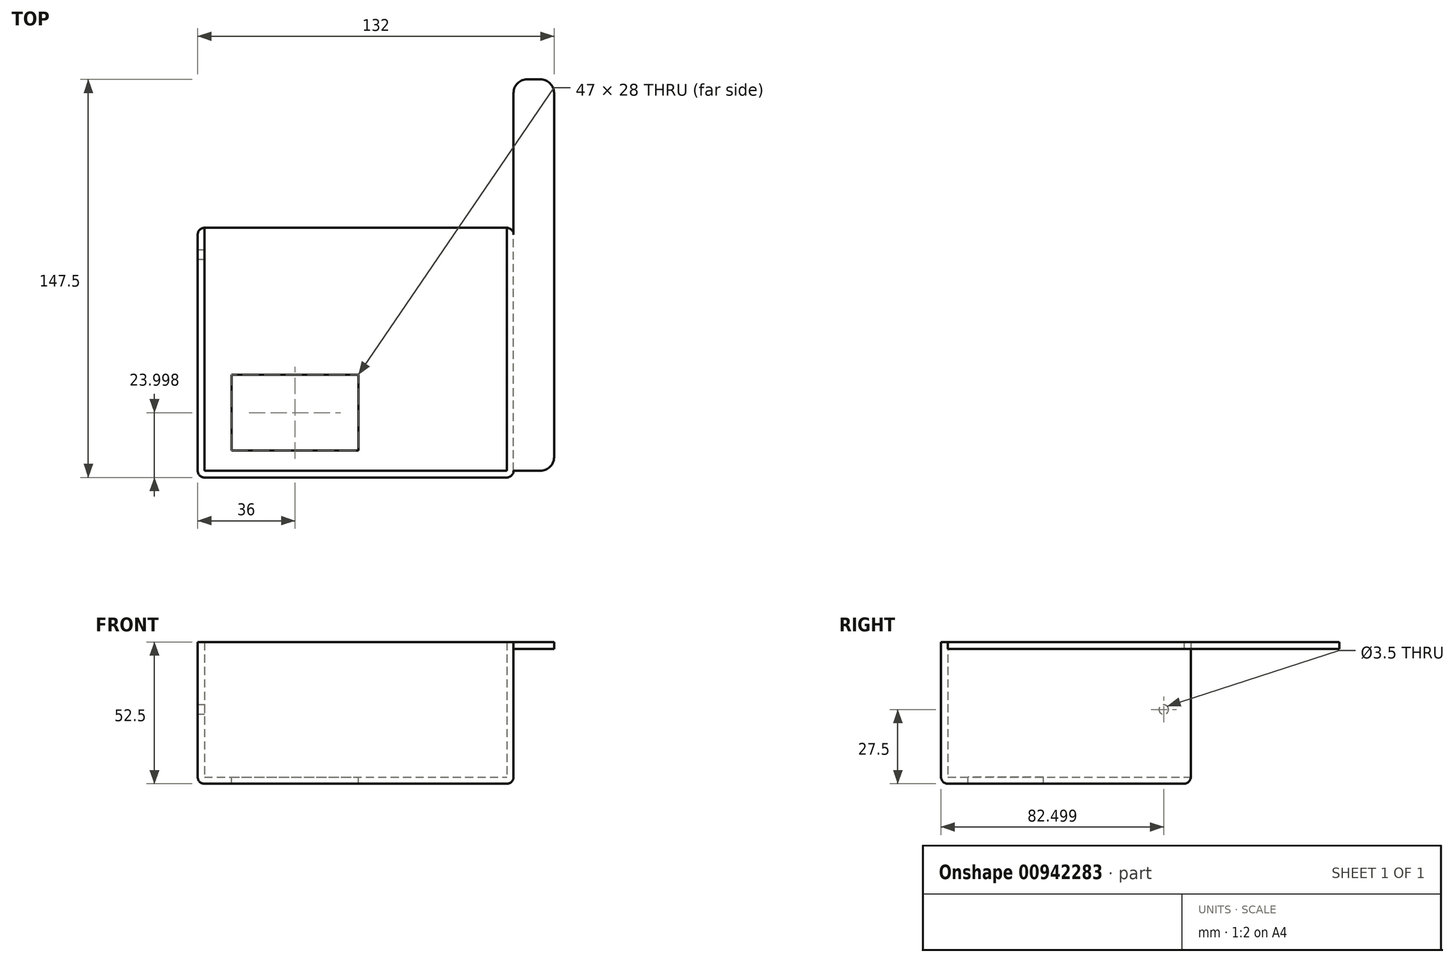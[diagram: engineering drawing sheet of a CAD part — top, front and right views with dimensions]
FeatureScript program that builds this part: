
annotation { "Feature Type Name" : "Feature", "Feature Type Description" : "" }
export const myFeature = defineFeature(function(context is Context, id is Id, definition is map)
    precondition{}
    {
        {
            var Q0;
            Q0=qCreatedBy(makeId("Top.planeOp"),FACE);
            var sketch = newSketch(context, id + "F0", { "sketchPlane" : qUnion([Q0])});
            skLineSegment(sketch, "E0.bottom", {"start": v(-58.5, 52.88) * mm, "end": v(58.5, 52.88) * mm});
            skLineSegment(sketch, "E0.top", {"start": v(-58.5, -39.62) * mm, "end": v(58.5, -39.62) * mm});
            skLineSegment(sketch, "E0.left", {"start": v(-58.5, 52.88) * mm, "end": v(-58.5, -39.62) * mm});
            skLineSegment(sketch, "E0.right", {"start": v(58.5, 52.88) * mm, "end": v(58.5, -39.62) * mm});
            skSolve(sketch);
        }
        {
            var Q0;
            Q0=makeQuery(id+"F0.imprint","IMPRINT",FACE,{"disambiguationData":[TD([[makeQuery(id+"F0.imprint","IMPRINT",EDGE,{"derivedFrom":sQuery(id+"F0.wireOp",EDGE,"E0.bottom")}),-1.0]])]});
            extrude(context, id + "F1", {"entities" : qUnion([Q0]), "depth" : 2.5 * mm, "offsetDistance" : 25 * mm});
        }
        {
            var Q0;
            Q0=makeQuery(id+"F1.opExtrude","CAP_FACE",FACE,{"disambiguationData":[OSD([sQuery(id+"F0.wireOp",EDGE,"E0.bottom"),sQuery(id+"F0.wireOp",EDGE,"E0.top"),sQuery(id+"F0.wireOp",EDGE,"E0.left"),sQuery(id+"F0.wireOp",EDGE,"E0.right")])],"isStart":false});
            var sketch = newSketch(context, id + "F2", { "sketchPlane" : qUnion([Q0])});
            skLineSegment(sketch, "E1.bottom", {"start": v(-46, -1.62) * mm, "end": v(1, -1.62) * mm});
            skLineSegment(sketch, "E1.top", {"start": v(-46, -29.62) * mm, "end": v(1, -29.62) * mm});
            skLineSegment(sketch, "E1.left", {"start": v(-46, -1.62) * mm, "end": v(-46, -29.62) * mm});
            skLineSegment(sketch, "E1.right", {"start": v(1, -1.62) * mm, "end": v(1, -29.62) * mm});
            skLineSegment(sketch, "E2.bottom", {"start": v(-58.5, -39.62) * mm, "end": v(58.5, -39.62) * mm});
            skLineSegment(sketch, "E2.top", {"start": v(-58.5, -37.12) * mm, "end": v(58.5, -37.12) * mm});
            skLineSegment(sketch, "E2.left", {"start": v(-58.5, -39.62) * mm, "end": v(-58.5, -37.12) * mm});
            skLineSegment(sketch, "E2.right", {"start": v(58.5, -39.62) * mm, "end": v(58.5, -37.12) * mm});
            skLineSegment(sketch, "E3.bottom", {"start": v(-58.5, -37.12) * mm, "end": v(-56, -37.12) * mm});
            skLineSegment(sketch, "E3.top", {"start": v(-58.5, 52.88) * mm, "end": v(-56, 52.88) * mm});
            skLineSegment(sketch, "E3.left", {"start": v(-58.5, -37.12) * mm, "end": v(-58.5, 52.88) * mm});
            skLineSegment(sketch, "E3.right", {"start": v(-56, -37.12) * mm, "end": v(-56, 52.88) * mm});
            skLineSegment(sketch, "E4.bottom", {"start": v(58.5, -37.12) * mm, "end": v(56, -37.12) * mm});
            skLineSegment(sketch, "E4.top", {"start": v(58.5, 52.88) * mm, "end": v(56, 52.88) * mm});
            skLineSegment(sketch, "E4.left", {"start": v(58.5, -37.12) * mm, "end": v(58.5, 52.88) * mm});
            skLineSegment(sketch, "E4.right", {"start": v(56, -37.12) * mm, "end": v(56, 52.88) * mm});
            skSolve(sketch);
        }
        {
            var Q0;
            Q0=makeQuery(id+"F2.imprint","IMPRINT",FACE,{"disambiguationData":[TD([[makeQuery(id+"F2.imprint","IMPRINT",EDGE,{"derivedFrom":sQuery(id+"F2.wireOp",EDGE,"E4.top")}),-1.0]])]});
            var Q1;
            Q1=makeQuery(id+"F2.imprint","IMPRINT",FACE,{"disambiguationData":[TD([[makeQuery(id+"F2.imprint","IMPRINT",EDGE,{"derivedFrom":sQuery(id+"F2.wireOp",EDGE,"E2.bottom")}),1.0]])]});
            var Q2;
            Q2=makeQuery(id+"F2.imprint","IMPRINT",FACE,{"disambiguationData":[TD([[makeQuery(id+"F2.imprint","IMPRINT",EDGE,{"derivedFrom":sQuery(id+"F2.wireOp",EDGE,"E3.top")}),-1.0]])]});
            extrude(context, id + "F3", {"entities" : qUnion([Q0, Q1, Q2]), "operationType" : NewBodyOperationType.ADD, "depth" : 50 * mm, "offsetDistance" : 25 * mm});
        }
        {
            var Q0;
            Q0=makeQuery(id+"F2.imprint","IMPRINT",FACE,{"disambiguationData":[TD([[makeQuery(id+"F2.imprint","IMPRINT",EDGE,{"derivedFrom":sQuery(id+"F2.wireOp",EDGE,"E1.bottom")}),-1.0]])]});
            extrude(context, id + "F4", {"entities" : qUnion([Q0]), "operationType" : NewBodyOperationType.REMOVE, "oppositeDirection" : true, "depth" : 25 * mm, "offsetDistance" : 25 * mm});
        }
        {
            var Q0;
            Q0=makeQuery(id+"F3.boolean.opBoolean","MERGE",FACE,{"derivedFrom":[makeQuery(id+"F1.opExtrude","SWEPT_FACE",FACE,{"disambiguationData":[OSD([sQuery(id+"F0.wireOp",EDGE,"E0.left")])]}),makeQuery(id+"F3.opExtrude","SWEPT_FACE",FACE,{"disambiguationData":[OSD([sQuery(id+"F2.wireOp",EDGE,"E2.left"),sQuery(id+"F2.wireOp",EDGE,"E3.left")])]})]});
            var sketch = newSketch(context, id + "F5", { "sketchPlane" : qUnion([Q0])});
            skCircle(sketch, "E5", {"center": v(-42.88, 27.5) * mm, "radius": 1.75 * mm});
            skSolve(sketch);
        }
        {
            var Q0;
            Q0 = qSketchRegion(id + "F5", true);
            extrude(context, id + "F6", {"entities" : qUnion([Q0]), "operationType" : NewBodyOperationType.REMOVE, "oppositeDirection" : true, "depth" : 25 * mm, "offsetDistance" : 25 * mm});
        }
        {
            var Q0;
            Q0=makeQuery(id+"F1.opExtrude","CAP_EDGE",EDGE,{"disambiguationData":[OSD([sQuery(id+"F0.wireOp",EDGE,"E0.left")])],"isStart":true});
            var Q1;
            Q1=makeQuery(id+"F3.boolean.opBoolean","MERGE",EDGE,{"derivedFrom":[makeQuery(id+"F1.opExtrude","SWEPT_EDGE",EDGE,{"disambiguationData":[OSD([sQuery(id+"F0.wireOp",EDGE,"E0.top"),sQuery(id+"F0.wireOp",EDGE,"E0.left")])]}),makeQuery(id+"F3.opExtrude","SWEPT_EDGE",EDGE,{"disambiguationData":[OSD([sQuery(id+"F2.wireOp",EDGE,"E2.bottom"),sQuery(id+"F2.wireOp",EDGE,"E2.left")])]})]});
            var Q2;
            Q2=makeQuery(id+"F1.opExtrude","CAP_EDGE",EDGE,{"disambiguationData":[OSD([sQuery(id+"F0.wireOp",EDGE,"E0.top")])],"isStart":true});
            var Q3;
            Q3=makeQuery(id+"F1.opExtrude","CAP_EDGE",EDGE,{"disambiguationData":[OSD([sQuery(id+"F0.wireOp",EDGE,"E0.right")])],"isStart":true});
            var Q4;
            Q4=makeQuery(id+"F3.boolean.opBoolean","MERGE",EDGE,{"derivedFrom":[makeQuery(id+"F1.opExtrude","SWEPT_EDGE",EDGE,{"disambiguationData":[OSD([sQuery(id+"F0.wireOp",EDGE,"E0.top"),sQuery(id+"F0.wireOp",EDGE,"E0.right")])]}),makeQuery(id+"F3.opExtrude","SWEPT_EDGE",EDGE,{"disambiguationData":[OSD([sQuery(id+"F2.wireOp",EDGE,"E2.bottom"),sQuery(id+"F2.wireOp",EDGE,"E2.right")])]})]});
            var Q5;
            Q5=makeQuery(id+"F1.opExtrude","CAP_EDGE",EDGE,{"disambiguationData":[OSD([sQuery(id+"F0.wireOp",EDGE,"E0.bottom")])],"isStart":true});
            var Q6;
            Q6=makeQuery(id+"F3.boolean.opBoolean","MERGE",EDGE,{"derivedFrom":[makeQuery(id+"F1.opExtrude","SWEPT_EDGE",EDGE,{"disambiguationData":[OSD([sQuery(id+"F0.wireOp",EDGE,"E0.bottom"),sQuery(id+"F0.wireOp",EDGE,"E0.left")])]}),makeQuery(id+"F3.opExtrude","SWEPT_EDGE",EDGE,{"disambiguationData":[OSD([sQuery(id+"F2.wireOp",EDGE,"E3.top"),sQuery(id+"F2.wireOp",EDGE,"E3.left")])]})]});
            var Q7;
            Q7=makeQuery(id+"F3.boolean.opBoolean","MERGE",EDGE,{"derivedFrom":[makeQuery(id+"F1.opExtrude","SWEPT_EDGE",EDGE,{"disambiguationData":[OSD([sQuery(id+"F0.wireOp",EDGE,"E0.bottom"),sQuery(id+"F0.wireOp",EDGE,"E0.right")])]}),makeQuery(id+"F3.opExtrude","SWEPT_EDGE",EDGE,{"disambiguationData":[OSD([sQuery(id+"F2.wireOp",EDGE,"E4.top"),sQuery(id+"F2.wireOp",EDGE,"E4.left")])]})]});
            fillet(context, id + "F7", {"entities" : qUnion([Q0, Q1, Q2, Q3, Q4, Q5, Q6, Q7]), "radius" : 2.5 * mm, "tangentPropagation" : true, "allowEdgeOverflow" : false});
        }
        {
            var Q0;
            Q0=makeQuery(id+"F3.boolean.opBoolean","MERGE",FACE,{"derivedFrom":[makeQuery(id+"F1.opExtrude","SWEPT_FACE",FACE,{"disambiguationData":[OSD([sQuery(id+"F0.wireOp",EDGE,"E0.right")])]}),makeQuery(id+"F3.opExtrude","SWEPT_FACE",FACE,{"disambiguationData":[OSD([sQuery(id+"F2.wireOp",EDGE,"E2.right"),sQuery(id+"F2.wireOp",EDGE,"E4.left")])]})]});
            var sketch = newSketch(context, id + "F8", { "sketchPlane" : qUnion([Q0])});
            skLineSegment(sketch, "E6.bottom", {"start": v(-37.12, 52.5) * mm, "end": v(107.88, 52.5) * mm});
            skLineSegment(sketch, "E6.top", {"start": v(-37.12, 50) * mm, "end": v(107.88, 50) * mm});
            skLineSegment(sketch, "E6.left", {"start": v(-37.12, 52.5) * mm, "end": v(-37.12, 50) * mm});
            skLineSegment(sketch, "E6.right", {"start": v(107.88, 52.5) * mm, "end": v(107.88, 50) * mm});
            skSolve(sketch);
        }
        {
            var Q0;
            {var subQ5=sQuery(id+"F8.wireOp",EDGE,"E6.right");Q0=makeQuery(id+"F8.imprint","IMPRINT",FACE,{"disambiguationData":[TD([[makeQuery(id+"F8.imprint","IMPRINT",EDGE,{"derivedFrom":subQ5}),-1.0]])]});}
            var Q1;
            {var subQ7=sQuery(id+"F8.wireOp",EDGE,"E6.left");Q1=makeQuery(id+"F8.imprint","IMPRINT",FACE,{"disambiguationData":[TD([[makeQuery(id+"F8.imprint","IMPRINT",EDGE,{"derivedFrom":subQ7}),1.0]])]});}
            extrude(context, id + "F9", {"entities" : qUnion([Q0, Q1]), "operationType" : NewBodyOperationType.ADD, "depth" : 15 * mm, "offsetDistance" : 25 * mm});
        }
        {
            var Q0;
            Q0=makeQuery(id+"F9.opExtrude","CAP_EDGE",EDGE,{"disambiguationData":[OSD([sQuery(id+"F8.wireOp",EDGE,"E6.right")])],"isStart":false});
            var Q1;
            Q1=makeQuery(id+"F9.opExtrude","CAP_EDGE",EDGE,{"disambiguationData":[OSD([sQuery(id+"F8.wireOp",EDGE,"E6.right")])],"isStart":true});
            var Q2;
            Q2=makeQuery(id+"F9.opExtrude","CAP_EDGE",EDGE,{"disambiguationData":[OSD([sQuery(id+"F8.wireOp",EDGE,"E6.left")])],"isStart":false});
            fillet(context, id + "F10", {"entities" : qUnion([Q0, Q1, Q2]), "radius" : 5 * mm, "tangentPropagation" : true, "allowEdgeOverflow" : false});
        }
    });
